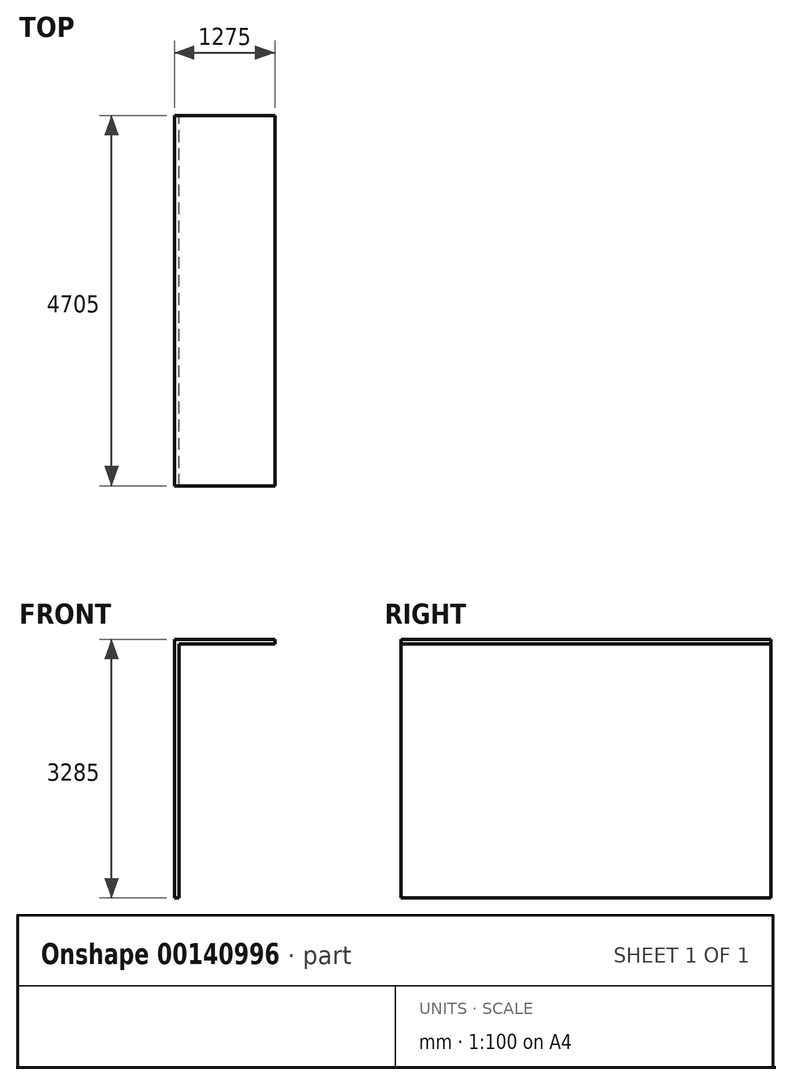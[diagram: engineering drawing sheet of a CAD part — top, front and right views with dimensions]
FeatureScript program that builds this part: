
annotation { "Feature Type Name" : "Feature", "Feature Type Description" : "" }
export const myFeature = defineFeature(function(context is Context, id is Id, definition is map)
    precondition{}
    {
        {
            var Q0;
            Q0=qCreatedBy(makeId("Front.planeOp"),FACE);
            var sketch = newSketch(context, id + "F0", { "sketchPlane" : qUnion([Q0])});
            skLineSegment(sketch, "E0", {"start": v(0, 3285) * mm, "end": v(-1275, 3285) * mm});
            skLineSegment(sketch, "E1", {"start": v(-1275, 3285) * mm, "end": v(-1275, 0) * mm});
            skLineSegment(sketch, "E2", {"start": v(-1275, 0) * mm, "end": v(-1215, 0) * mm});
            skLineSegment(sketch, "E3", {"start": v(-1215, 0) * mm, "end": v(-1215, 3225) * mm});
            skLineSegment(sketch, "E4", {"start": v(0, 3285) * mm, "end": v(0, 3225) * mm});
            skLineSegment(sketch, "E5", {"start": v(-1215, 3225) * mm, "end": v(0, 3225) * mm});
            skSolve(sketch);
        }
        {
            var Q0;
            Q0 = qSketchRegion(id + "F0", true);
            extrude(context, id + "F1", {"entities" : qUnion([Q0]), "depth" : 4705 * mm});
        }
    });
